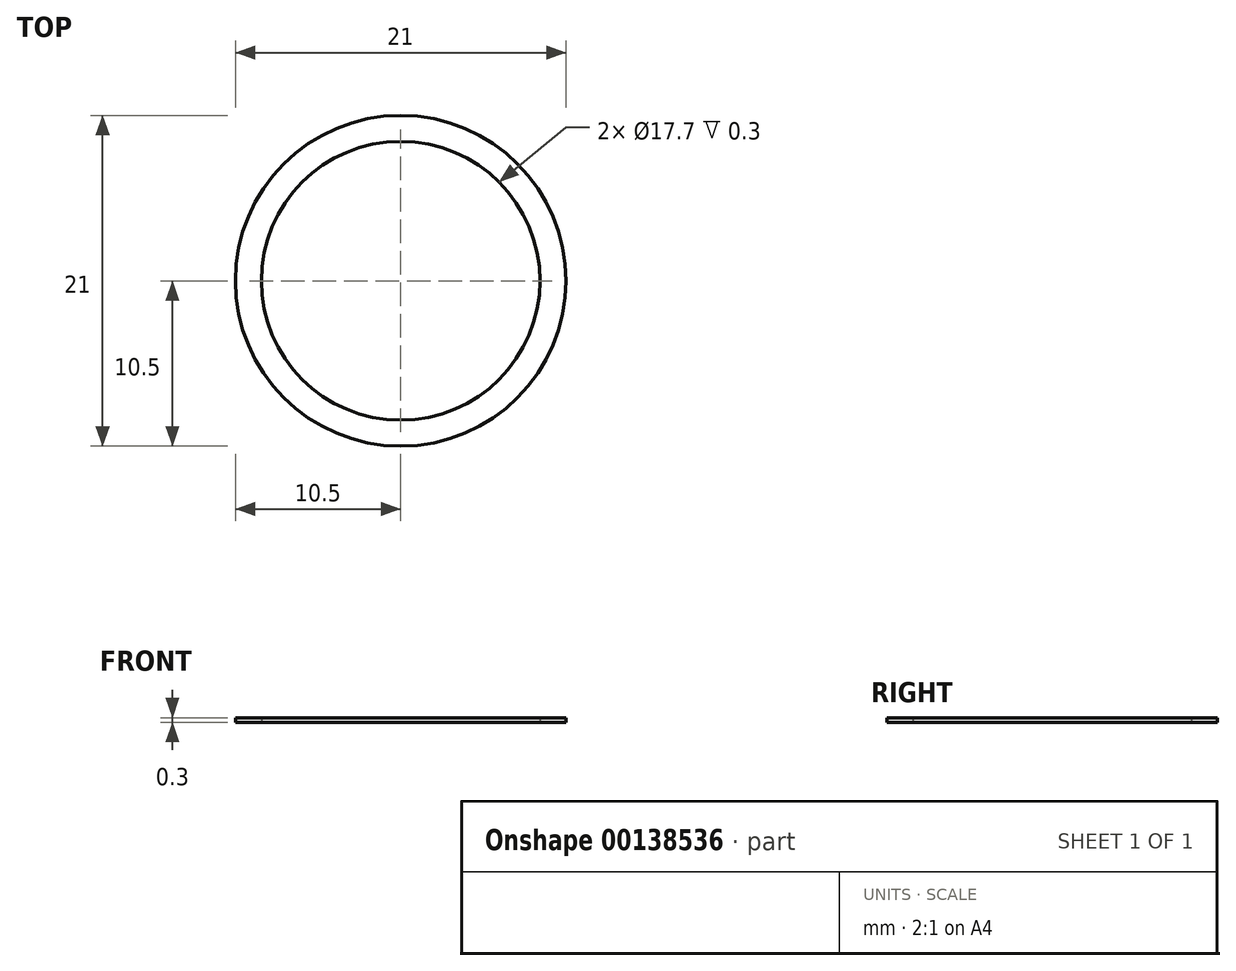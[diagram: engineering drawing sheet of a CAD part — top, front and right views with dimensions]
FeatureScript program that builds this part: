
annotation { "Feature Type Name" : "Feature", "Feature Type Description" : "" }
export const myFeature = defineFeature(function(context is Context, id is Id, definition is map)
    precondition{}
    {
        {
            var Q0;
            Q0=qCreatedBy(makeId("Top.planeOp"),FACE);
            var sketch = newSketch(context, id + "F0", { "sketchPlane" : qUnion([Q0])});
            skCircle(sketch, "E0", {"center": v(0, 0) * mm, "radius": 10.5 * mm});
            skCircle(sketch, "E1", {"center": v(0, 0) * mm, "radius": 8.85 * mm});
            skSolve(sketch);
        }
        {
            var Q0;
            Q0 = qSketchRegion(id + "F0", true);
            extrude(context, id + "F1", {"entities" : qUnion([Q0]), "depth" : .3 * mm});
        }
    });
